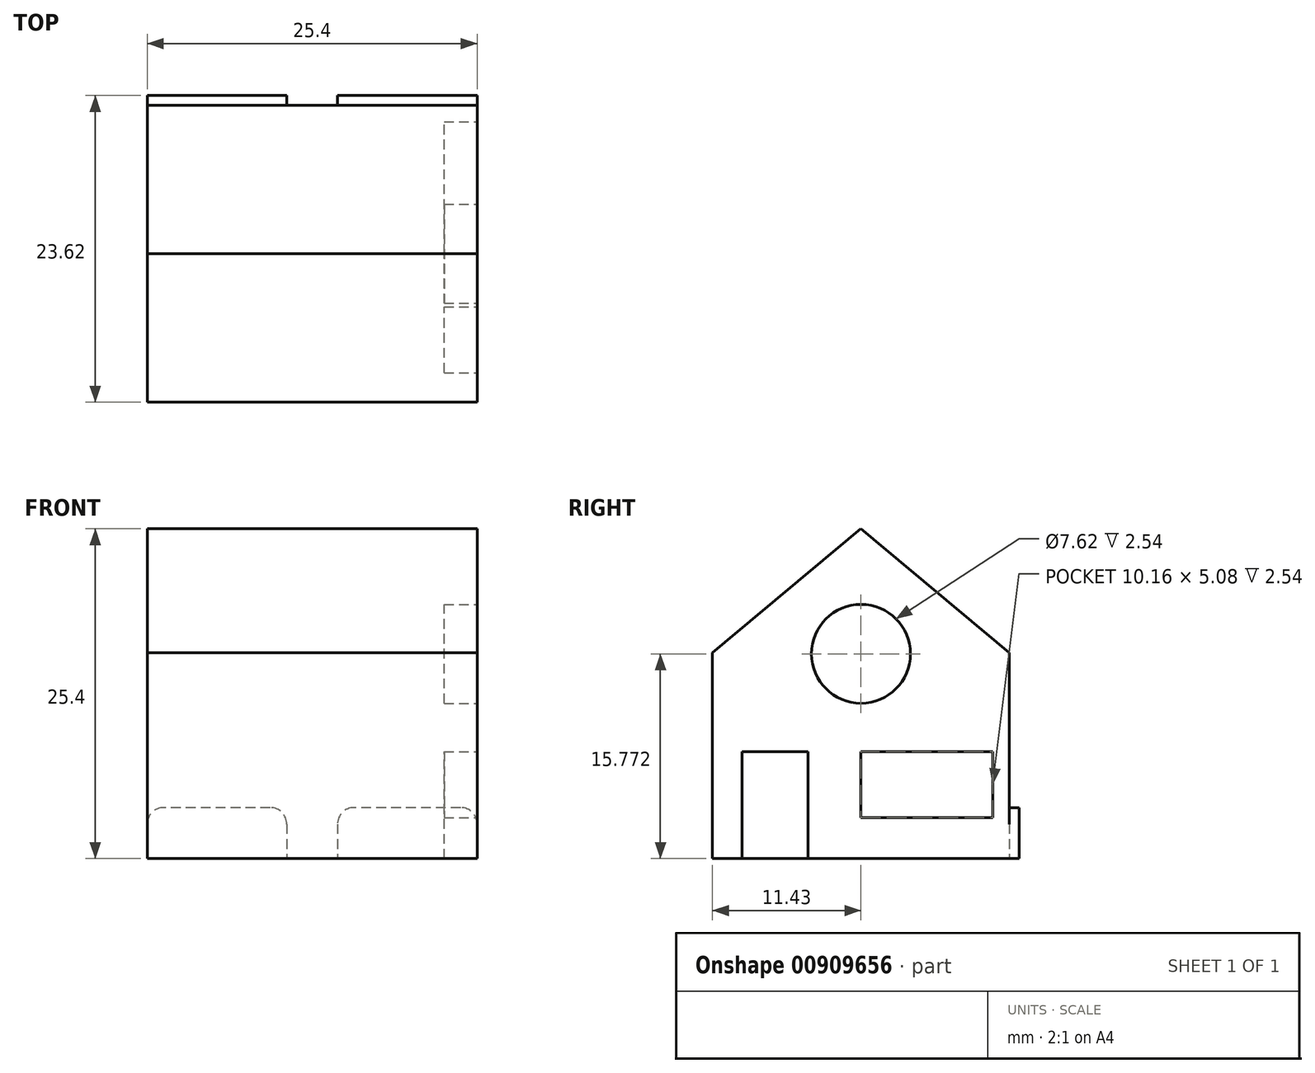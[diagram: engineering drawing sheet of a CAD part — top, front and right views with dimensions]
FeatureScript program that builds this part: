
annotation { "Feature Type Name" : "Feature", "Feature Type Description" : "" }
export const myFeature = defineFeature(function(context is Context, id is Id, definition is map)
    precondition{}
    {
        {
            var Q0;
            Q0=qCreatedBy(makeId("Right.planeOp"),FACE);
            var sketch = newSketch(context, id + "F0", { "sketchPlane" : qUnion([Q0])});
            skLineSegment(sketch, "E0.bottom", {"start": v(-11.43, 7.61) * mm, "end": v(11.43, 7.61) * mm});
            skLineSegment(sketch, "E0.top", {"start": v(-11.43, -8.25) * mm, "end": v(11.43, -8.25) * mm});
            skLineSegment(sketch, "E0.left", {"start": v(-11.43, 7.61) * mm, "end": v(-11.43, -8.25) * mm});
            skLineSegment(sketch, "E0.right", {"start": v(11.43, 7.61) * mm, "end": v(11.43, -8.25) * mm});
            skLineSegment(sketch, "E1", {"start": v(-11.43, 7.61) * mm, "end": v(0, 17.15) * mm});
            skLineSegment(sketch, "E2", {"start": v(0, 17.15) * mm, "end": v(11.43, 7.61) * mm});
            skSolve(sketch);
        }
        {
            var Q0;
            Q0 = qSketchRegion(id + "F0", true);
            extrude(context, id + "F1", {"entities" : qUnion([Q0]), "endBound" : BoundingType.SYMMETRIC, "depth" : 25.4 * mm, "offsetDistance" : 25.4 * mm});
        }
        {
            var Q0;
            Q0=makeQuery(id+"F1.opExtrude","CAP_FACE",FACE,{"disambiguationData":[OSD([sQuery(id+"F0.wireOp",EDGE,"E0.top"),sQuery(id+"F0.wireOp",EDGE,"E0.left"),sQuery(id+"F0.wireOp",EDGE,"E0.right"),sQuery(id+"F0.wireOp",EDGE,"E1"),sQuery(id+"F0.wireOp",EDGE,"E2")])],"isStart":false});
            var sketch = newSketch(context, id + "F2", { "sketchPlane" : qUnion([Q0])});
            skLineSegment(sketch, "E3.bottom", {"start": v(-9.15, -8.25) * mm, "end": v(-4.07, -8.25) * mm});
            skLineSegment(sketch, "E3.top", {"start": v(-9.15, 0) * mm, "end": v(-4.07, 0) * mm});
            skLineSegment(sketch, "E3.left", {"start": v(-9.15, -8.25) * mm, "end": v(-9.15, 0) * mm});
            skLineSegment(sketch, "E3.right", {"start": v(-4.07, -8.25) * mm, "end": v(-4.07, 0) * mm});
            skLineSegment(sketch, "E4.bottom", {"start": v(0, 0) * mm, "end": v(10.16, 0) * mm});
            skLineSegment(sketch, "E4.top", {"start": v(0, -5.08) * mm, "end": v(10.16, -5.08) * mm});
            skLineSegment(sketch, "E4.left", {"start": v(0, 0) * mm, "end": v(0, -5.08) * mm});
            skLineSegment(sketch, "E4.right", {"start": v(10.16, 0) * mm, "end": v(10.16, -5.08) * mm});
            skCircle(sketch, "E5", {"center": v(0, 7.52) * mm, "radius": 3.81 * mm});
            skSolve(sketch);
        }
        {
            var Q0;
            Q0 = qSketchRegion(id + "F2", true);
            extrude(context, id + "F3", {"entities" : qUnion([Q0]), "operationType" : NewBodyOperationType.REMOVE, "oppositeDirection" : true, "depth" : 2.54 * mm, "offsetDistance" : 25.4 * mm});
        }
        {
            var Q0;
            Q0=makeQuery(id+"F1.opExtrude","SWEPT_FACE",FACE,{"disambiguationData":[OSD([sQuery(id+"F0.wireOp",EDGE,"E0.right")])]});
            var sketch = newSketch(context, id + "F4", { "sketchPlane" : qUnion([Q0])});
            skLineSegment(sketch, "E6.bottom", {"start": v(-11.43, -4.32) * mm, "end": v(-3.25, -4.32) * mm});
            skLineSegment(sketch, "E6.top", {"start": v(-12.7, -8.25) * mm, "end": v(-1.98, -8.25) * mm});
            skLineSegment(sketch, "E6.left", {"start": v(-12.7, -5.6) * mm, "end": v(-12.7, -8.25) * mm});
            skLineSegment(sketch, "E6.right", {"start": v(-1.98, -5.6) * mm, "end": v(-1.98, -8.25) * mm});
            skPoint(sketch, "E7.visualSharp", {"position": v(-12.7, -4.32) * mm});
            skArc(sketch, "E7.filletArc", {"start": v(-11.43, -4.32) * mm, "mid": v(-12.33, -4.7) * mm, "end": v(-12.7, -5.6) * mm});
            skPoint(sketch, "E8.visualSharp", {"position": v(-1.98, -4.32) * mm});
            skArc(sketch, "E8.filletArc", {"start": v(-1.98, -5.6) * mm, "mid": v(-2.35, -4.7) * mm, "end": v(-3.25, -4.32) * mm});
            skLineSegment(sketch, "E9.bottom", {"start": v(3.23, -4.32) * mm, "end": v(5.06, -4.32) * mm});
            skLineSegment(sketch, "E9.top", {"start": v(1.96, -8.25) * mm, "end": v(6.33, -8.25) * mm});
            skLineSegment(sketch, "E9.left", {"start": v(1.96, -5.6) * mm, "end": v(1.96, -8.25) * mm});
            skLineSegment(sketch, "E9.right", {"start": v(6.33, -5.6) * mm, "end": v(6.33, -8.25) * mm});
            skPoint(sketch, "E10.visualSharp", {"position": v(1.96, -4.32) * mm});
            skArc(sketch, "E10.filletArc", {"start": v(3.23, -4.32) * mm, "mid": v(2.33, -4.7) * mm, "end": v(1.96, -5.6) * mm});
            skPoint(sketch, "E11.visualSharp", {"position": v(6.33, -4.32) * mm});
            skArc(sketch, "E11.filletArc", {"start": v(6.33, -5.6) * mm, "mid": v(5.96, -4.7) * mm, "end": v(5.06, -4.32) * mm});
            skLineSegment(sketch, "E12.MirrorCS", {"start": v(-3.23, -4.32) * mm, "end": v(-5.06, -4.32) * mm});
            skArc(sketch, "E13.MirrorCS", {"start": v(-3.23, -4.32) * mm, "mid": v(-2.33, -4.7) * mm, "end": v(-1.96, -5.6) * mm});
            skArc(sketch, "E14.MirrorCS", {"start": v(-6.33, -5.6) * mm, "mid": v(-5.96, -4.7) * mm, "end": v(-5.06, -4.32) * mm});
            skLineSegment(sketch, "E15.MirrorCS", {"start": v(-1.96, -8.25) * mm, "end": v(-6.33, -8.25) * mm});
            skLineSegment(sketch, "E16.MirrorCS", {"start": v(-1.96, -5.6) * mm, "end": v(-1.96, -8.25) * mm});
            skLineSegment(sketch, "E17.MirrorCS", {"start": v(-6.33, -5.6) * mm, "end": v(-6.33, -8.25) * mm});
            skPoint(sketch, "E18.MirrorP", {"position": v(-1.96, -4.32) * mm});
            skPoint(sketch, "E19.MirrorP", {"position": v(-6.33, -4.32) * mm});
            skLineSegment(sketch, "E20.MirrorCS", {"start": v(11.43, -4.32) * mm, "end": v(3.25, -4.32) * mm});
            skArc(sketch, "E21.MirrorCS", {"start": v(11.43, -4.32) * mm, "mid": v(12.33, -4.7) * mm, "end": v(12.7, -5.6) * mm});
            skPoint(sketch, "E22.MirrorP", {"position": v(12.7, -4.32) * mm});
            skArc(sketch, "E23.MirrorCS", {"start": v(1.98, -5.6) * mm, "mid": v(2.35, -4.7) * mm, "end": v(3.25, -4.32) * mm});
            skLineSegment(sketch, "E24.MirrorCS", {"start": v(12.7, -5.6) * mm, "end": v(12.7, -8.25) * mm});
            skPoint(sketch, "E25.MirrorP", {"position": v(1.98, -4.32) * mm});
            skLineSegment(sketch, "E26.MirrorCS", {"start": v(12.7, -8.25) * mm, "end": v(1.98, -8.25) * mm});
            skLineSegment(sketch, "E27.MirrorCS", {"start": v(1.98, -5.6) * mm, "end": v(1.98, -8.25) * mm});
            skSolve(sketch);
        }
        {
            var Q0;
            Q0 = qSketchRegion(id + "F4", true);
            extrude(context, id + "F5", {"entities" : qUnion([Q0]), "operationType" : NewBodyOperationType.ADD, "depth" : 0.76 * mm, "offsetDistance" : 25.4 * mm});
        }
    });
